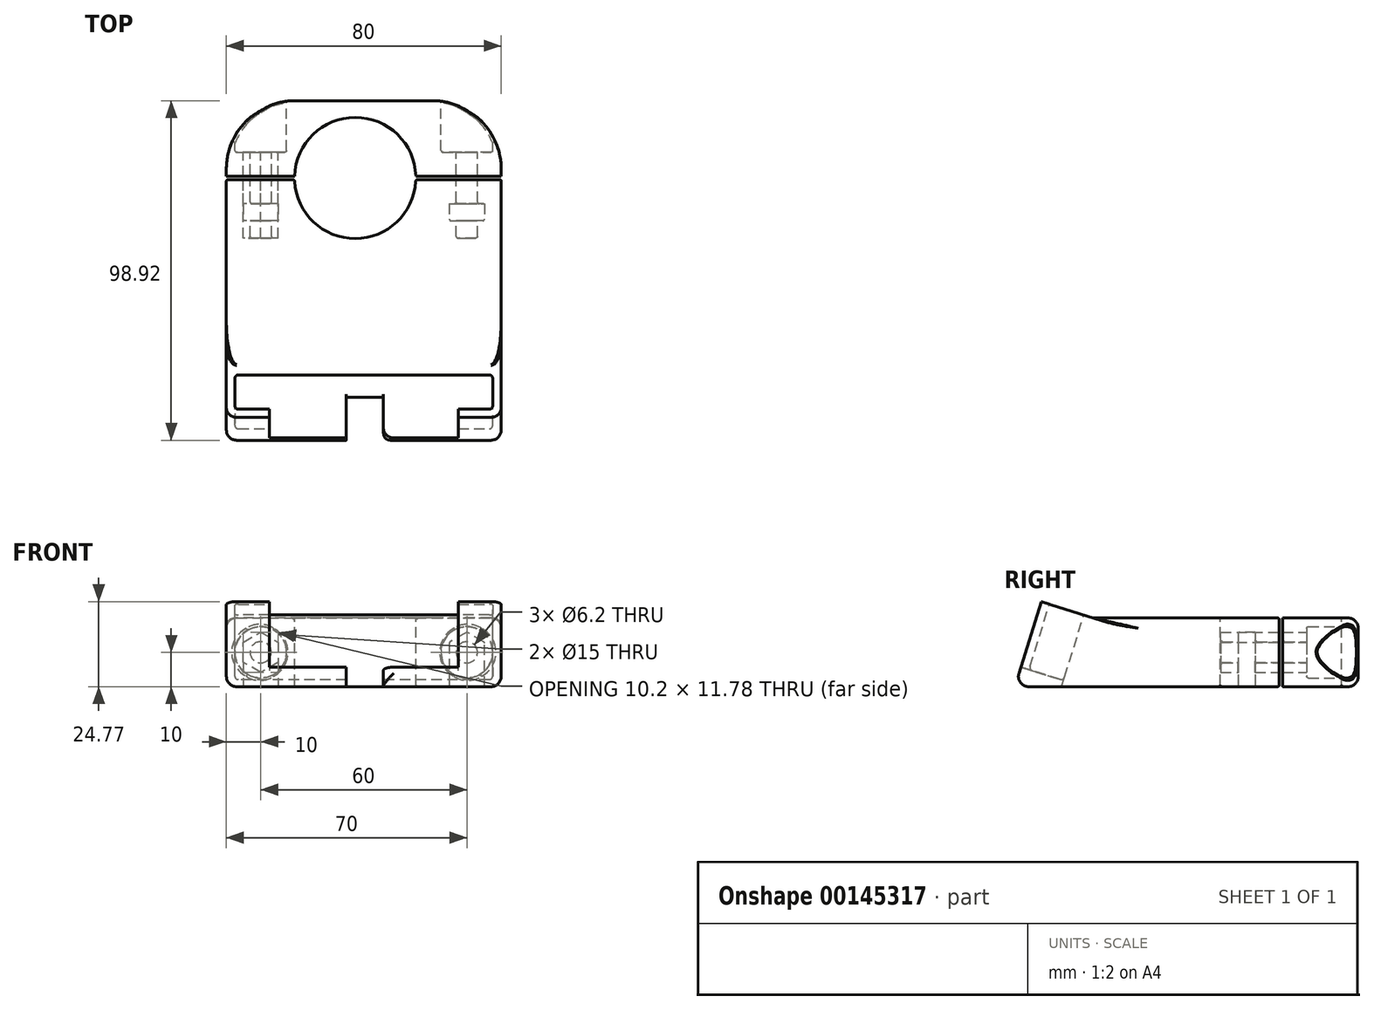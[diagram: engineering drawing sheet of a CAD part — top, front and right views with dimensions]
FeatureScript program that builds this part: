
annotation { "Feature Type Name" : "Feature", "Feature Type Description" : "" }
export const myFeature = defineFeature(function(context is Context, id is Id, definition is map)
    precondition{}
    {
        {
            var Q0;
            Q0=qCreatedBy(makeId("Right.planeOp"),FACE);
            var sketch = newSketch(context, id + "F0", { "sketchPlane" : qUnion([Q0])});
            skLineSegment(sketch, "E0", {"start": v(-34.54, 0) * mm, "end": v(65.46, 0) * mm});
            skLineSegment(sketch, "E1", {"start": v(65.46, 0) * mm, "end": v(65.46, 20) * mm});
            skLineSegment(sketch, "E2", {"start": v(65.46, 20) * mm, "end": v(-11.54, 20) * mm});
            skLineSegment(sketch, "E3", {"start": v(-11.54, 20) * mm, "end": v(-26.81, 24.77) * mm});
            skLineSegment(sketch, "E4", {"start": v(-26.81, 24.77) * mm, "end": v(-34.54, 0) * mm});
            skLineSegment(sketch, "E5", {"start": v(25.46, 20) * mm, "end": v(25.46, 148.67) * mm});
            skLineSegment(sketch, "E6", {"start": v(-14.4, 20.9) * mm, "end": v(40.27, 196.16) * mm});
            skSolve(sketch);
        }
        {
            var Q0;
            Q0=makeQuery(id+"F0.imprint","IMPRINT",FACE,{"disambiguationData":[TD([[makeQuery(id+"F0.imprint","IMPRINT",EDGE,{"derivedFrom":sQuery(id+"F0.wireOp",EDGE,"E0")}),1.0]])]});
            extrude(context, id + "F1", {"entities" : qUnion([Q0]), "endBound" : BoundingType.SYMMETRIC, "depth" : 80 * mm});
        }
        {
            var Q0;
            Q0=makeQuery(id+"F1.opExtrude","SWEPT_FACE",FACE,{"disambiguationData":[OSD([sQuery(id+"F0.wireOp",EDGE,"E3")])]});
            var sketch = newSketch(context, id + "F2", { "sketchPlane" : qUnion([Q0])});
            skLineSegment(sketch, "E7", {"start": v(-37.5, -19.97) * mm, "end": v(-37.5, -30.47) * mm});
            skLineSegment(sketch, "E8", {"start": v(-37.5, -30.47) * mm, "end": v(37.5, -30.47) * mm});
            skLineSegment(sketch, "E9", {"start": v(37.5, -30.47) * mm, "end": v(37.5, -19.97) * mm});
            skLineSegment(sketch, "E10", {"start": v(37.5, -19.97) * mm, "end": v(-37.5, -19.97) * mm});
            skLineSegment(sketch, "E11", {"start": v(-27.5, -32.97) * mm, "end": v(-27.5, -30.47) * mm});
            skLineSegment(sketch, "E12", {"start": v(-27.5, -30.47) * mm, "end": v(27.5, -30.47) * mm});
            skLineSegment(sketch, "E13", {"start": v(27.5, -30.47) * mm, "end": v(27.5, -32.97) * mm});
            skLineSegment(sketch, "E14", {"start": v(27.5, -32.97) * mm, "end": v(-27.5, -32.97) * mm});
            skSolve(sketch);
        }
        {
            var Q0;
            Q0=makeQuery(id+"F2.imprint","IMPRINT",FACE,{"disambiguationData":[TD([[makeQuery(id+"F2.imprint","IMPRINT",EDGE,{"derivedFrom":sQuery(id+"F2.wireOp",EDGE,"E7")}),1.0]])]});
            extrude(context, id + "F3", {"entities" : qUnion([Q0]), "operationType" : NewBodyOperationType.REMOVE, "oppositeDirection" : true, "depth" : 20 * mm});
        }
        {
            var Q0;
            Q0=makeQuery(id+"F2.imprint","IMPRINT",FACE,{"disambiguationData":[TD([[makeQuery(id+"F2.imprint","IMPRINT",EDGE,{"derivedFrom":sQuery(id+"F2.wireOp",EDGE,"E11")}),-1.0]])]});
            extrude(context, id + "F4", {"entities" : qUnion([Q0]), "operationType" : NewBodyOperationType.REMOVE, "oppositeDirection" : true, "depth" : 20 * mm});
        }
        {
            var Q0;
            {var subQ0=sQuery(id+"F2.wireOp",EDGE,"E12");Q0=makeQuery(id+"F4.boolean.opBoolean","MERGE",FACE,{"derivedFrom":[makeQuery(id+"F3.boolean.opBoolean","COPY",FACE,{"derivedFrom":makeQuery(id+"F3.opExtrude","CAP_FACE",FACE,{"disambiguationData":[OSD([sQuery(id+"F2.wireOp",EDGE,"E7"),sQuery(id+"F2.wireOp",EDGE,"E8"),sQuery(id+"F2.wireOp",EDGE,"E9"),sQuery(id+"F2.wireOp",EDGE,"E10"),subQ0])],"isStart":false})}),makeQuery(id+"F4.opExtrude","CAP_FACE",FACE,{"disambiguationData":[OSD([sQuery(id+"F2.wireOp",EDGE,"E11"),subQ0,sQuery(id+"F2.wireOp",EDGE,"E13"),sQuery(id+"F2.wireOp",EDGE,"E14")])],"isStart":false})]});}
            var sketch = newSketch(context, id + "F5", { "sketchPlane" : qUnion([Q0])});
            skLineSegment(sketch, "E15", {"start": v(-5.1, -32.97) * mm, "end": v(-5.1, -19.97) * mm});
            skLineSegment(sketch, "E16", {"start": v(-5.1, -19.97) * mm, "end": v(5.72, -19.97) * mm});
            skLineSegment(sketch, "E17", {"start": v(5.72, -19.97) * mm, "end": v(5.72, -32.97) * mm});
            skLineSegment(sketch, "E18", {"start": v(5.72, -32.97) * mm, "end": v(-5.1, -32.97) * mm});
            skSolve(sketch);
        }
        {
            var Q0;
            Q0=makeQuery(id+"F5.imprint","IMPRINT",FACE,{"disambiguationData":[TD([[makeQuery(id+"F5.imprint","IMPRINT",EDGE,{"derivedFrom":sQuery(id+"F5.wireOp",EDGE,"E15")}),-1.0]])]});
            extrude(context, id + "F6", {"entities" : qUnion([Q0]), "operationType" : NewBodyOperationType.REMOVE, "oppositeDirection" : true, "depth" : 25 * mm});
        }
        {
            var Q0;
            Q0=makeQuery(id+"F1.opExtrude","SWEPT_FACE",FACE,{"disambiguationData":[OSD([sQuery(id+"F0.wireOp",EDGE,"E2")])]});
            var sketch = newSketch(context, id + "F7", { "sketchPlane" : qUnion([Q0])});
            skCircle(sketch, "E19", {"center": v(-2.5, 42.96) * mm, "radius": 17.65 * mm});
            skLineSegment(sketch, "E20", {"start": v(-40, 43.46) * mm, "end": v(40, 43.46) * mm});
            skLineSegment(sketch, "E21", {"start": v(-40, 42.46) * mm, "end": v(40, 42.46) * mm});
            skSolve(sketch);
        }
        {
            var Q0;
            {var subQ0=sQuery(id+"F7.wireOp",EDGE,"E21");var subQ1=sQuery(id+"F7.wireOp",EDGE,"E19");var subQ2=makeQuery(id+"F7.imprint","INTERSECT",VERTEX,{"disambiguationData":[OD(0.0)],"derivedFrom":[subQ1,subQ0]});Q0=makeQuery(id+"F7.imprint","IMPRINT",FACE,{"disambiguationData":[TD([[makeQuery(id+"F7.imprint","IMPRINT",EDGE,{"disambiguationData":[TD([[subQ2,-1.0]])],"derivedFrom":subQ1}),1.0]])]});}
            var Q1;
            {var subQ0=sQuery(id+"F7.wireOp",EDGE,"E20");var subQ1=sQuery(id+"F7.wireOp",EDGE,"E19");var subQ2=makeQuery(id+"F7.imprint","INTERSECT",VERTEX,{"disambiguationData":[OD(0.0)],"derivedFrom":[subQ1,subQ0]});Q1=makeQuery(id+"F7.imprint","IMPRINT",FACE,{"disambiguationData":[TD([[makeQuery(id+"F7.imprint","IMPRINT",EDGE,{"disambiguationData":[TD([[subQ2,1.0]])],"derivedFrom":subQ1}),1.0]])]});}
            var Q2;
            {var subQ0=sQuery(id+"F7.wireOp",EDGE,"E20");var subQ1=sQuery(id+"F7.wireOp",EDGE,"E19");var subQ2=makeQuery(id+"F7.imprint","INTERSECT",VERTEX,{"disambiguationData":[OD(0.0)],"derivedFrom":[subQ1,subQ0]});Q2=makeQuery(id+"F7.imprint","IMPRINT",FACE,{"disambiguationData":[TD([[makeQuery(id+"F7.imprint","IMPRINT",EDGE,{"disambiguationData":[TD([[subQ2,-1.0]])],"derivedFrom":subQ1}),1.0]])]});}
            extrude(context, id + "F8", {"entities" : qUnion([Q0, Q1, Q2]), "operationType" : NewBodyOperationType.REMOVE, "oppositeDirection" : true, "depth" : 25 * mm});
        }
        {
            var Q0;
            Q0=makeQuery(id+"F1.opExtrude","SWEPT_FACE",FACE,{"disambiguationData":[OSD([sQuery(id+"F0.wireOp",EDGE,"E1")])]});
            var sketch = newSketch(context, id + "F9", { "sketchPlane" : qUnion([Q0])});
            skCircle(sketch, "E22", {"center": v(-30, 10) * mm, "radius": 3.1 * mm});
            skPoint(sketch, "E22.centerSnap0", {"position": v(-40, 10) * mm});
            skLineSegment(sketch, "E23", {"start": v(0, 0) * mm, "end": v(0, 27.17) * mm});
            skPoint(sketch, "E23.endSnap0", {"position": v(0, 20) * mm});
            skCircle(sketch, "E24", {"center": v(-30, 10) * mm, "radius": 7.5 * mm});
            skCircle(sketch, "E25.cCircle", {"center": v(-30, 10) * mm, "radius": 5.1 * mm, "construction": true});
            skLineSegment(sketch, "E25.0", {"start": v(-24.9, 12.94) * mm, "end": v(-24.9, 7.06) * mm});
            skLineSegment(sketch, "E25.1", {"start": v(-24.9, 7.06) * mm, "end": v(-30, 4.11) * mm});
            skLineSegment(sketch, "E25.2", {"start": v(-30, 4.11) * mm, "end": v(-35.1, 7.06) * mm});
            skLineSegment(sketch, "E25.3", {"start": v(-35.1, 7.06) * mm, "end": v(-35.1, 12.94) * mm});
            skLineSegment(sketch, "E25.4", {"start": v(-35.1, 12.94) * mm, "end": v(-30, 15.89) * mm});
            skLineSegment(sketch, "E25.5", {"start": v(-30, 15.89) * mm, "end": v(-24.9, 12.94) * mm});
            skPoint(sketch, "E25.0.midPoint", {"position": v(-24.9, 10) * mm});
            skCircle(sketch, "E26.MirrorC", {"center": v(30, 10) * mm, "radius": 3.1 * mm});
            skCircle(sketch, "E27.MirrorC", {"center": v(30, 10) * mm, "radius": 5.1 * mm, "construction": true});
            skLineSegment(sketch, "E28.MirrorCS", {"start": v(24.9, 7.06) * mm, "end": v(30, 4.11) * mm});
            skLineSegment(sketch, "E29.MirrorCS", {"start": v(24.9, 12.94) * mm, "end": v(24.9, 7.06) * mm});
            skLineSegment(sketch, "E30.MirrorCS", {"start": v(30, 15.89) * mm, "end": v(24.9, 12.94) * mm});
            skLineSegment(sketch, "E31.MirrorCS", {"start": v(35.1, 12.94) * mm, "end": v(30, 15.89) * mm});
            skLineSegment(sketch, "E32.MirrorCS", {"start": v(35.1, 7.06) * mm, "end": v(35.1, 12.94) * mm});
            skLineSegment(sketch, "E33.MirrorCS", {"start": v(30, 4.11) * mm, "end": v(35.1, 7.06) * mm});
            skCircle(sketch, "E34.MirrorC", {"center": v(30, 10) * mm, "radius": 7.5 * mm});
            skSolve(sketch);
        }
        {
            var Q0;
            Q0=makeQuery(id+"F9.imprint","IMPRINT",FACE,{"disambiguationData":[TD([[makeQuery(id+"F9.imprint","IMPRINT",EDGE,{"derivedFrom":sQuery(id+"F9.wireOp",EDGE,"E22")}),1.0]])]});
            var Q1;
            Q1=makeQuery(id+"F9.imprint","IMPRINT",FACE,{"disambiguationData":[TD([[makeQuery(id+"F9.imprint","IMPRINT",EDGE,{"derivedFrom":sQuery(id+"F9.wireOp",EDGE,"E26.MirrorC")}),-1.0]])]});
            extrude(context, id + "F10", {"entities" : qUnion([Q0, Q1]), "operationType" : NewBodyOperationType.REMOVE, "oppositeDirection" : true, "depth" : 40 * mm});
        }
        {
            var Q0;
            Q0=makeQuery(id+"F9.imprint","IMPRINT",FACE,{"disambiguationData":[TD([[makeQuery(id+"F9.imprint","IMPRINT",EDGE,{"derivedFrom":sQuery(id+"F9.wireOp",EDGE,"E22")}),-1.0]])]});
            var Q1;
            Q1=makeQuery(id+"F9.imprint","IMPRINT",FACE,{"disambiguationData":[TD([[makeQuery(id+"F9.imprint","IMPRINT",EDGE,{"derivedFrom":sQuery(id+"F9.wireOp",EDGE,"E26.MirrorC")}),1.0]])]});
            extrude(context, id + "F11", {"entities" : qUnion([Q0, Q1]), "operationType" : NewBodyOperationType.REMOVE, "oppositeDirection" : true, "depth" : 35 * mm});
        }
        {
            var Q0;
            Q0=makeQuery(id+"F9.imprint","IMPRINT",FACE,{"disambiguationData":[TD([[makeQuery(id+"F9.imprint","IMPRINT",EDGE,{"derivedFrom":sQuery(id+"F9.wireOp",EDGE,"E22")}),-1.0]])]});
            var Q1;
            Q1=makeQuery(id+"F9.imprint","IMPRINT",FACE,{"disambiguationData":[TD([[makeQuery(id+"F9.imprint","IMPRINT",EDGE,{"derivedFrom":sQuery(id+"F9.wireOp",EDGE,"E26.MirrorC")}),1.0]])]});
            extrude(context, id + "F12", {"entities" : qUnion([Q0, Q1]), "operationType" : NewBodyOperationType.ADD, "oppositeDirection" : true, "depth" : 30 * mm});
        }
        {
            var Q0;
            Q0=makeQuery(id+"F9.imprint","IMPRINT",FACE,{"disambiguationData":[TD([[makeQuery(id+"F9.imprint","IMPRINT",EDGE,{"derivedFrom":sQuery(id+"F9.wireOp",EDGE,"E24")}),1.0]])]});
            var Q1;
            Q1=makeQuery(id+"F9.imprint","IMPRINT",FACE,{"disambiguationData":[TD([[makeQuery(id+"F9.imprint","IMPRINT",EDGE,{"derivedFrom":sQuery(id+"F9.wireOp",EDGE,"E22")}),-1.0]])]});
            var Q2;
            Q2=makeQuery(id+"F9.imprint","IMPRINT",FACE,{"disambiguationData":[TD([[makeQuery(id+"F9.imprint","IMPRINT",EDGE,{"derivedFrom":sQuery(id+"F9.wireOp",EDGE,"E26.MirrorC")}),1.0]])]});
            var Q3;
            Q3=makeQuery(id+"F9.imprint","IMPRINT",FACE,{"disambiguationData":[TD([[makeQuery(id+"F9.imprint","IMPRINT",EDGE,{"derivedFrom":sQuery(id+"F9.wireOp",EDGE,"E28.MirrorCS")}),-1.0]])]});
            extrude(context, id + "F13", {"entities" : qUnion([Q0, Q1, Q2, Q3]), "operationType" : NewBodyOperationType.REMOVE, "oppositeDirection" : true, "depth" : 15 * mm});
        }
        {
            var Q0;
            Q0=makeQuery(id+"F1.opExtrude","SWEPT_FACE",FACE,{"disambiguationData":[OSD([sQuery(id+"F0.wireOp",EDGE,"E0")])]});
            var sketch = newSketch(context, id + "F14", { "sketchPlane" : qUnion([Q0])});
            skLineSegment(sketch, "E35.bottom", {"start": v(24.9, -35.46) * mm, "end": v(35.1, -35.46) * mm});
            skLineSegment(sketch, "E35.top", {"start": v(24.9, -30.46) * mm, "end": v(35.1, -30.46) * mm});
            skLineSegment(sketch, "E35.left", {"start": v(24.9, -35.46) * mm, "end": v(24.9, -30.46) * mm});
            skLineSegment(sketch, "E35.right", {"start": v(35.1, -35.46) * mm, "end": v(35.1, -30.46) * mm});
            skPoint(sketch, "E35.middle", {"position": v(30, -32.96) * mm});
            skLineSegment(sketch, "E36", {"start": v(0, -65.46) * mm, "end": v(0, 26.3) * mm});
            skLineSegment(sketch, "E37.MirrorCS", {"start": v(-24.9, -30.46) * mm, "end": v(-35.1, -30.46) * mm});
            skLineSegment(sketch, "E38.MirrorCS", {"start": v(-35.1, -35.46) * mm, "end": v(-35.1, -30.46) * mm});
            skLineSegment(sketch, "E39.MirrorCS", {"start": v(-24.9, -35.46) * mm, "end": v(-35.1, -35.46) * mm});
            skLineSegment(sketch, "E40.MirrorCS", {"start": v(-24.9, -35.46) * mm, "end": v(-24.9, -30.46) * mm});
            skSolve(sketch);
        }
        {
            var Q0;
            Q0=makeQuery(id+"F14.imprint","IMPRINT",FACE,{"disambiguationData":[TD([[makeQuery(id+"F14.imprint","IMPRINT",EDGE,{"derivedFrom":sQuery(id+"F14.wireOp",EDGE,"E37.MirrorCS")}),1.0]])]});
            var Q1;
            Q1=makeQuery(id+"F14.imprint","IMPRINT",FACE,{"disambiguationData":[TD([[makeQuery(id+"F14.imprint","IMPRINT",EDGE,{"derivedFrom":sQuery(id+"F14.wireOp",EDGE,"E35.bottom")}),1.0]])]});
            extrude(context, id + "F15", {"entities" : qUnion([Q0, Q1]), "operationType" : NewBodyOperationType.REMOVE, "oppositeDirection" : true, "depth" : 10 * mm});
        }
        {
            var Q0;
            {var subQ0=sQuery(id+"F7.wireOp",EDGE,"E20");var subQ1=sQuery(id+"F7.wireOp",EDGE,"E19");var subQ2=makeQuery(id+"F7.imprint","INTERSECT",VERTEX,{"disambiguationData":[OD(1.0)],"derivedFrom":[subQ1,subQ0]});Q0=makeQuery(id+"F7.imprint","IMPRINT",FACE,{"disambiguationData":[TD([[makeQuery(id+"F7.imprint","IMPRINT",EDGE,{"disambiguationData":[TD([[subQ2,1.0]])],"derivedFrom":subQ1}),-1.0]])]});}
            var Q1;
            {var subQ0=sQuery(id+"F7.wireOp",EDGE,"E20");var subQ1=sQuery(id+"F7.wireOp",EDGE,"E19");var subQ2=makeQuery(id+"F7.imprint","INTERSECT",VERTEX,{"disambiguationData":[OD(0.0)],"derivedFrom":[subQ1,subQ0]});Q1=makeQuery(id+"F7.imprint","IMPRINT",FACE,{"disambiguationData":[TD([[makeQuery(id+"F7.imprint","IMPRINT",EDGE,{"disambiguationData":[TD([[subQ2,-1.0]])],"derivedFrom":subQ1}),-1.0]])]});}
            extrude(context, id + "F16", {"entities" : qUnion([Q0, Q1]), "operationType" : NewBodyOperationType.REMOVE, "endBound" : BoundingType.THROUGH_ALL, "oppositeDirection" : true, "depth" : 25 * mm});
        }
        {
            var Q0;
            Q0=makeQuery(id+"F1.opExtrude","CAP_EDGE",EDGE,{"disambiguationData":[OSD([sQuery(id+"F0.wireOp",EDGE,"E1")])],"isStart":false});
            var Q1;
            Q1=makeQuery(id+"F1.opExtrude","CAP_EDGE",EDGE,{"disambiguationData":[OSD([sQuery(id+"F0.wireOp",EDGE,"E1")])],"isStart":true});
            fillet(context, id + "F17", {"entities" : qUnion([Q0, Q1]), "radius" : 20 * mm, "tangentPropagation" : true, "allowEdgeOverflow" : false});
        }
        {
            var Q0;
            {var subQ0=sQuery(id+"F0.wireOp",EDGE,"E3");var subQ1=sQuery(id+"F0.wireOp",EDGE,"E2");var subQ3=makeQuery(id+"F1.opExtrude","CAP_EDGE",EDGE,{"disambiguationData":[OSD([subQ1])],"isStart":false});Q0=makeQuery(id+"F16.boolean.opBoolean","SPLIT",EDGE,{"disambiguationData":[TD([makeQuery(id+"F1.opExtrude","SWEPT_FACE",FACE,{"disambiguationData":[OSD([subQ0])]})])],"derivedFrom":subQ3});}
            var Q1;
            {var subQ1=sQuery(id+"F0.wireOp",EDGE,"E2");var subQ2=makeQuery(id+"F1.opExtrude","CAP_EDGE",EDGE,{"disambiguationData":[OSD([subQ1])],"isStart":false});var subQ3=sQuery(id+"F0.wireOp",EDGE,"E1");Q1=makeQuery(id+"F16.boolean.opBoolean","SPLIT",EDGE,{"disambiguationData":[TD([makeQuery(id+"F1.opExtrude","SWEPT_FACE",FACE,{"disambiguationData":[OSD([subQ3])]})])],"derivedFrom":subQ2});}
            var Q2;
            {var subQ1=sQuery(id+"F0.wireOp",EDGE,"E1");var subQ3=sQuery(id+"F0.wireOp",EDGE,"E2");Q2=makeQuery(id+"F17.opFillet","BLEND_EDGE",EDGE,{"blendedFrom":[makeQuery(id+"F1.opExtrude","CAP_EDGE",EDGE,{"disambiguationData":[OSD([subQ1])],"isStart":false}),makeQuery(id+"F16.boolean.opBoolean","SPLIT",FACE,{"disambiguationData":[TD([makeQuery(id+"F1.opExtrude","SWEPT_FACE",FACE,{"disambiguationData":[OSD([subQ1])]})])],"derivedFrom":makeQuery(id+"F1.opExtrude","SWEPT_FACE",FACE,{"disambiguationData":[OSD([subQ3])]})})],"blendedInto":[makeQuery(id+"F16.boolean.opBoolean","SPLIT",FACE,{"disambiguationData":[TD([makeQuery(id+"F1.opExtrude","SWEPT_FACE",FACE,{"disambiguationData":[OSD([subQ1])]})])],"derivedFrom":makeQuery(id+"F1.opExtrude","SWEPT_FACE",FACE,{"disambiguationData":[OSD([subQ3])]})})]});}
            var Q3;
            {var subQ0=sQuery(id+"F0.wireOp",EDGE,"E3");var subQ1=sQuery(id+"F0.wireOp",EDGE,"E2");var subQ3=makeQuery(id+"F1.opExtrude","CAP_EDGE",EDGE,{"disambiguationData":[OSD([subQ1])],"isStart":true});Q3=makeQuery(id+"F16.boolean.opBoolean","SPLIT",EDGE,{"disambiguationData":[TD([makeQuery(id+"F1.opExtrude","SWEPT_FACE",FACE,{"disambiguationData":[OSD([subQ0])]})])],"derivedFrom":subQ3});}
            var Q4;
            Q4=makeQuery(id+"F6.boolean.opBoolean","COPY",EDGE,{"derivedFrom":makeQuery(id+"F6.opExtrude","SWEPT_EDGE",EDGE,{"disambiguationData":[OSD([sQuery(id+"F2.wireOp",EDGE,"E14"),sQuery(id+"F5.wireOp",EDGE,"E15"),sQuery(id+"F5.wireOp",EDGE,"E18")])]})});
            var Q5;
            Q5=makeQuery(id+"F6.boolean.opBoolean","COPY",EDGE,{"derivedFrom":makeQuery(id+"F6.opExtrude","SWEPT_EDGE",EDGE,{"disambiguationData":[OSD([sQuery(id+"F2.wireOp",EDGE,"E14"),sQuery(id+"F5.wireOp",EDGE,"E17"),sQuery(id+"F5.wireOp",EDGE,"E18")])]})});
            var Q6;
            Q6=makeQuery(id+"F4.boolean.opBoolean","COPY",EDGE,{"derivedFrom":makeQuery(id+"F4.opExtrude","CAP_EDGE",EDGE,{"disambiguationData":[OSD([sQuery(id+"F2.wireOp",EDGE,"E13")])],"isStart":true})});
            var Q7;
            Q7=makeQuery(id+"F4.boolean.opBoolean","COPY",EDGE,{"derivedFrom":makeQuery(id+"F4.opExtrude","CAP_EDGE",EDGE,{"disambiguationData":[OSD([sQuery(id+"F2.wireOp",EDGE,"E11")])],"isStart":true})});
            var Q8;
            {var subQ0=sQuery(id+"F0.wireOp",EDGE,"E0");var subQ1=sQuery(id+"F0.wireOp",EDGE,"E4");Q8=makeQuery(id+"F6.boolean.opBoolean","SPLIT",EDGE,{"disambiguationData":[TD([makeQuery(id+"F6.opExtrude","SWEPT_FACE",FACE,{"disambiguationData":[OSD([sQuery(id+"F5.wireOp",EDGE,"E15")])]})])],"derivedFrom":makeQuery(id+"F1.opExtrude","SWEPT_EDGE",EDGE,{"disambiguationData":[OSD([subQ0,subQ1])]})});}
            var Q9;
            {var subQ0=sQuery(id+"F0.wireOp",EDGE,"E0");var subQ1=sQuery(id+"F0.wireOp",EDGE,"E4");Q9=makeQuery(id+"F6.boolean.opBoolean","SPLIT",EDGE,{"disambiguationData":[TD([makeQuery(id+"F6.opExtrude","SWEPT_FACE",FACE,{"disambiguationData":[OSD([sQuery(id+"F5.wireOp",EDGE,"E17")])]})])],"derivedFrom":makeQuery(id+"F1.opExtrude","SWEPT_EDGE",EDGE,{"disambiguationData":[OSD([subQ0,subQ1])]})});}
            var Q10;
            {var subQ0=sQuery(id+"F0.wireOp",EDGE,"E0");var subQ1=sQuery(id+"F0.wireOp",EDGE,"E4");Q10=makeQuery(id+"F16.boolean.opBoolean","SPLIT",EDGE,{"disambiguationData":[TD([makeQuery(id+"F1.opExtrude","SWEPT_FACE",FACE,{"disambiguationData":[OSD([subQ1])]})])],"derivedFrom":makeQuery(id+"F1.opExtrude","CAP_EDGE",EDGE,{"disambiguationData":[OSD([subQ0])],"isStart":true})});}
            var Q11;
            {var subQ0=sQuery(id+"F0.wireOp",EDGE,"E0");var subQ1=sQuery(id+"F0.wireOp",EDGE,"E4");Q11=makeQuery(id+"F16.boolean.opBoolean","SPLIT",EDGE,{"disambiguationData":[TD([makeQuery(id+"F1.opExtrude","SWEPT_FACE",FACE,{"disambiguationData":[OSD([subQ1])]})])],"derivedFrom":makeQuery(id+"F1.opExtrude","CAP_EDGE",EDGE,{"disambiguationData":[OSD([subQ0])],"isStart":false})});}
            var Q12;
            {var subQ2=sQuery(id+"F0.wireOp",EDGE,"E1");var subQ3=sQuery(id+"F0.wireOp",EDGE,"E0");Q12=makeQuery(id+"F16.boolean.opBoolean","SPLIT",EDGE,{"disambiguationData":[TD([makeQuery(id+"F1.opExtrude","SWEPT_FACE",FACE,{"disambiguationData":[OSD([subQ2])]})])],"derivedFrom":makeQuery(id+"F1.opExtrude","CAP_EDGE",EDGE,{"disambiguationData":[OSD([subQ3])],"isStart":false})});}
            var Q13;
            Q13=makeQuery(id+"F1.opExtrude","CAP_EDGE",EDGE,{"disambiguationData":[OSD([sQuery(id+"F0.wireOp",EDGE,"E4")])],"isStart":false});
            var Q14;
            Q14=makeQuery(id+"F1.opExtrude","CAP_EDGE",EDGE,{"disambiguationData":[OSD([sQuery(id+"F0.wireOp",EDGE,"E4")])],"isStart":true});
            fillet(context, id + "F18", {"entities" : qUnion([Q0, Q1, Q2, Q3, Q4, Q5, Q6, Q7, Q8, Q9, Q10, Q11, Q12, Q13, Q14]), "radius" : 3 * mm, "tangentPropagation" : true, "allowEdgeOverflow" : false});
        }
        {
            var Q0;
            {var subQ0=sQuery(id+"F7.wireOp",EDGE,"E20");Q0=makeQuery(id+"F16.boolean.opBoolean","COPY",EDGE,{"derivedFrom":makeQuery(id+"F16.opExtrude","CAP_EDGE",EDGE,{"disambiguationData":[OSD([subQ0]),TDD([makeQuery(id+"F7.imprint","IMPRINT",EDGE,{"disambiguationData":[TD([[makeQuery(id+"F7.imprint","INTERSECT",VERTEX,{"derivedFrom":[makeQuery(id+"F1.opExtrude","CAP_EDGE",EDGE,{"disambiguationData":[OSD([sQuery(id+"F0.wireOp",EDGE,"E2")])],"isStart":true}),subQ0]}),-1.0]])],"derivedFrom":subQ0})])],"isStart":true})});}
            var Q1;
            {var subQ0=sQuery(id+"F7.wireOp",EDGE,"E20");var subQ1=sQuery(id+"F7.wireOp",EDGE,"E19");Q1=makeQuery(id+"F16.boolean.opBoolean","COPY",EDGE,{"derivedFrom":makeQuery(id+"F16.opExtrude","SWEPT_EDGE",EDGE,{"disambiguationData":[OSD([subQ1,subQ0]),TDD([makeQuery(id+"F7.imprint","INTERSECT",VERTEX,{"disambiguationData":[OD(0.0)],"derivedFrom":[subQ1,subQ0]})])]})});}
            var Q2;
            {var subQ0=sQuery(id+"F7.wireOp",EDGE,"E20");var subQ1=sQuery(id+"F7.wireOp",EDGE,"E19");Q2=makeQuery(id+"F16.boolean.opBoolean","COPY",EDGE,{"derivedFrom":makeQuery(id+"F16.opExtrude","SWEPT_EDGE",EDGE,{"disambiguationData":[OSD([subQ1,subQ0]),TDD([makeQuery(id+"F7.imprint","INTERSECT",VERTEX,{"disambiguationData":[OD(1.0)],"derivedFrom":[subQ1,subQ0]})])]})});}
            var Q3;
            {var subQ0=sQuery(id+"F7.wireOp",EDGE,"E20");Q3=makeQuery(id+"F16.boolean.opBoolean","COPY",EDGE,{"derivedFrom":makeQuery(id+"F16.opExtrude","CAP_EDGE",EDGE,{"disambiguationData":[OSD([subQ0]),TDD([makeQuery(id+"F7.imprint","IMPRINT",EDGE,{"disambiguationData":[TD([[makeQuery(id+"F7.imprint","INTERSECT",VERTEX,{"derivedFrom":[makeQuery(id+"F1.opExtrude","CAP_EDGE",EDGE,{"disambiguationData":[OSD([sQuery(id+"F0.wireOp",EDGE,"E2")])],"isStart":false}),subQ0]}),1.0]])],"derivedFrom":subQ0})])],"isStart":true})});}
            var Q4;
            {var subQ0=sQuery(id+"F7.wireOp",EDGE,"E21");var subQ1=sQuery(id+"F0.wireOp",EDGE,"E2");Q4=makeQuery(id+"F16.boolean.opBoolean","COPY",EDGE,{"derivedFrom":makeQuery(id+"F16.opExtrude","SWEPT_EDGE",EDGE,{"disambiguationData":[OSD([subQ1,subQ0]),TDD([makeQuery(id+"F7.imprint","INTERSECT",VERTEX,{"derivedFrom":[makeQuery(id+"F1.opExtrude","CAP_EDGE",EDGE,{"disambiguationData":[OSD([subQ1])],"isStart":false}),subQ0]})])]})});}
            var Q5;
            {var subQ0=sQuery(id+"F7.wireOp",EDGE,"E21");var subQ1=sQuery(id+"F7.wireOp",EDGE,"E19");Q5=makeQuery(id+"F16.boolean.opBoolean","COPY",EDGE,{"derivedFrom":makeQuery(id+"F16.opExtrude","SWEPT_EDGE",EDGE,{"disambiguationData":[OSD([subQ1,subQ0]),TDD([makeQuery(id+"F7.imprint","INTERSECT",VERTEX,{"disambiguationData":[OD(1.0)],"derivedFrom":[subQ1,subQ0]})])]})});}
            var Q6;
            {var subQ0=sQuery(id+"F7.wireOp",EDGE,"E21");var subQ1=sQuery(id+"F7.wireOp",EDGE,"E19");Q6=makeQuery(id+"F16.boolean.opBoolean","COPY",EDGE,{"derivedFrom":makeQuery(id+"F16.opExtrude","SWEPT_EDGE",EDGE,{"disambiguationData":[OSD([subQ1,subQ0]),TDD([makeQuery(id+"F7.imprint","INTERSECT",VERTEX,{"disambiguationData":[OD(0.0)],"derivedFrom":[subQ1,subQ0]})])]})});}
            var Q7;
            {var subQ0=sQuery(id+"F7.wireOp",EDGE,"E21");Q7=makeQuery(id+"F16.boolean.opBoolean","INTERSECT",EDGE,{"derivedFrom":[makeQuery(id+"F1.opExtrude","SWEPT_FACE",FACE,{"disambiguationData":[OSD([sQuery(id+"F0.wireOp",EDGE,"E0")])]}),makeQuery(id+"F16.opExtrude","SWEPT_FACE",FACE,{"disambiguationData":[OSD([subQ0]),TDD([makeQuery(id+"F7.imprint","IMPRINT",EDGE,{"disambiguationData":[TD([[makeQuery(id+"F7.imprint","INTERSECT",VERTEX,{"derivedFrom":[makeQuery(id+"F1.opExtrude","CAP_EDGE",EDGE,{"disambiguationData":[OSD([sQuery(id+"F0.wireOp",EDGE,"E2")])],"isStart":true}),subQ0]}),-1.0]])],"derivedFrom":subQ0})])]})]});}
            var Q8;
            {var subQ0=makeQuery(id+"F1.opExtrude","SWEPT_FACE",FACE,{"disambiguationData":[OSD([sQuery(id+"F0.wireOp",EDGE,"E0")])]});var subQ1=sQuery(id+"F7.wireOp",EDGE,"E19");var subQ2=makeQuery(id+"F8.opExtrude","SWEPT_FACE",FACE,{"disambiguationData":[OSD([subQ1])]});var subQ3=sQuery(id+"F7.wireOp",EDGE,"E20");var subQ4=sQuery(id+"F0.wireOp",EDGE,"E2");Q8=makeQuery(id+"F16.boolean.opBoolean","SPLIT",EDGE,{"disambiguationData":[TD([makeQuery(id+"F16.opExtrude","SWEPT_FACE",FACE,{"disambiguationData":[OSD([subQ3]),TDD([makeQuery(id+"F7.imprint","IMPRINT",EDGE,{"disambiguationData":[TD([[makeQuery(id+"F7.imprint","INTERSECT",VERTEX,{"derivedFrom":[makeQuery(id+"F1.opExtrude","CAP_EDGE",EDGE,{"disambiguationData":[OSD([subQ4])],"isStart":true}),subQ3]}),-1.0]])],"derivedFrom":subQ3})])]})])],"derivedFrom":makeQuery(id+"F8.boolean.opBoolean","INTERSECT",EDGE,{"derivedFrom":[subQ0,subQ2]})});}
            var Q9;
            {var subQ0=makeQuery(id+"F1.opExtrude","SWEPT_FACE",FACE,{"disambiguationData":[OSD([sQuery(id+"F0.wireOp",EDGE,"E0")])]});var subQ1=sQuery(id+"F7.wireOp",EDGE,"E19");var subQ2=makeQuery(id+"F8.opExtrude","SWEPT_FACE",FACE,{"disambiguationData":[OSD([subQ1])]});var subQ3=sQuery(id+"F7.wireOp",EDGE,"E21");var subQ4=sQuery(id+"F0.wireOp",EDGE,"E2");Q9=makeQuery(id+"F16.boolean.opBoolean","SPLIT",EDGE,{"disambiguationData":[TD([makeQuery(id+"F16.opExtrude","SWEPT_FACE",FACE,{"disambiguationData":[OSD([subQ3]),TDD([makeQuery(id+"F7.imprint","IMPRINT",EDGE,{"disambiguationData":[TD([[makeQuery(id+"F7.imprint","INTERSECT",VERTEX,{"derivedFrom":[makeQuery(id+"F1.opExtrude","CAP_EDGE",EDGE,{"disambiguationData":[OSD([subQ4])],"isStart":true}),subQ3]}),-1.0]])],"derivedFrom":subQ3})])]})])],"derivedFrom":makeQuery(id+"F8.boolean.opBoolean","INTERSECT",EDGE,{"derivedFrom":[subQ0,subQ2]})});}
            var Q10;
            Q10=makeQuery(id+"F15.boolean.opBoolean","COPY",EDGE,{"derivedFrom":makeQuery(id+"F15.opExtrude","CAP_EDGE",EDGE,{"disambiguationData":[OSD([sQuery(id+"F14.wireOp",EDGE,"E37.MirrorCS")])],"isStart":true})});
            var Q11;
            Q11=makeQuery(id+"F15.boolean.opBoolean","COPY",EDGE,{"derivedFrom":makeQuery(id+"F15.opExtrude","CAP_EDGE",EDGE,{"disambiguationData":[OSD([sQuery(id+"F14.wireOp",EDGE,"E40.MirrorCS")])],"isStart":true})});
            var Q12;
            Q12=makeQuery(id+"F15.boolean.opBoolean","COPY",EDGE,{"derivedFrom":makeQuery(id+"F15.opExtrude","CAP_EDGE",EDGE,{"disambiguationData":[OSD([sQuery(id+"F14.wireOp",EDGE,"E39.MirrorCS")])],"isStart":true})});
            var Q13;
            Q13=makeQuery(id+"F15.boolean.opBoolean","COPY",EDGE,{"derivedFrom":makeQuery(id+"F15.opExtrude","CAP_EDGE",EDGE,{"disambiguationData":[OSD([sQuery(id+"F14.wireOp",EDGE,"E38.MirrorCS")])],"isStart":true})});
            var Q14;
            Q14=makeQuery(id+"F15.boolean.opBoolean","COPY",EDGE,{"derivedFrom":makeQuery(id+"F15.opExtrude","CAP_EDGE",EDGE,{"disambiguationData":[OSD([sQuery(id+"F14.wireOp",EDGE,"E35.bottom")])],"isStart":true})});
            var Q15;
            Q15=makeQuery(id+"F15.boolean.opBoolean","COPY",EDGE,{"derivedFrom":makeQuery(id+"F15.opExtrude","CAP_EDGE",EDGE,{"disambiguationData":[OSD([sQuery(id+"F14.wireOp",EDGE,"E35.left")])],"isStart":true})});
            var Q16;
            Q16=makeQuery(id+"F15.boolean.opBoolean","COPY",EDGE,{"derivedFrom":makeQuery(id+"F15.opExtrude","CAP_EDGE",EDGE,{"disambiguationData":[OSD([sQuery(id+"F14.wireOp",EDGE,"E35.top")])],"isStart":true})});
            var Q17;
            Q17=makeQuery(id+"F15.boolean.opBoolean","COPY",EDGE,{"derivedFrom":makeQuery(id+"F15.opExtrude","CAP_EDGE",EDGE,{"disambiguationData":[OSD([sQuery(id+"F14.wireOp",EDGE,"E35.right")])],"isStart":true})});
            var Q18;
            {var subQ0=sQuery(id+"F0.wireOp",EDGE,"E2");var subQ1=sQuery(id+"F7.wireOp",EDGE,"E19");var subQ2=sQuery(id+"F7.wireOp",EDGE,"E21");Q18=makeQuery(id+"F16.boolean.opBoolean","SPLIT",EDGE,{"disambiguationData":[TD([makeQuery(id+"F16.opExtrude","SWEPT_FACE",FACE,{"disambiguationData":[OSD([subQ2]),TDD([makeQuery(id+"F7.imprint","IMPRINT",EDGE,{"disambiguationData":[TD([[makeQuery(id+"F7.imprint","INTERSECT",VERTEX,{"derivedFrom":[makeQuery(id+"F1.opExtrude","CAP_EDGE",EDGE,{"disambiguationData":[OSD([subQ0])],"isStart":true}),subQ2]}),-1.0]])],"derivedFrom":subQ2})])]})])],"derivedFrom":makeQuery(id+"F8.boolean.opBoolean","COPY",EDGE,{"derivedFrom":makeQuery(id+"F8.opExtrude","CAP_EDGE",EDGE,{"disambiguationData":[OSD([subQ1])],"isStart":true})})});}
            var Q19;
            {var subQ0=sQuery(id+"F0.wireOp",EDGE,"E2");var subQ1=sQuery(id+"F7.wireOp",EDGE,"E19");var subQ2=sQuery(id+"F7.wireOp",EDGE,"E20");Q19=makeQuery(id+"F16.boolean.opBoolean","SPLIT",EDGE,{"disambiguationData":[TD([makeQuery(id+"F16.opExtrude","SWEPT_FACE",FACE,{"disambiguationData":[OSD([subQ2]),TDD([makeQuery(id+"F7.imprint","IMPRINT",EDGE,{"disambiguationData":[TD([[makeQuery(id+"F7.imprint","INTERSECT",VERTEX,{"derivedFrom":[makeQuery(id+"F1.opExtrude","CAP_EDGE",EDGE,{"disambiguationData":[OSD([subQ0])],"isStart":true}),subQ2]}),-1.0]])],"derivedFrom":subQ2})])]})])],"derivedFrom":makeQuery(id+"F8.boolean.opBoolean","COPY",EDGE,{"derivedFrom":makeQuery(id+"F8.opExtrude","CAP_EDGE",EDGE,{"disambiguationData":[OSD([subQ1])],"isStart":true})})});}
            var Q20;
            Q20=makeQuery(id+"F13.boolean.opBoolean","COPY",EDGE,{"derivedFrom":makeQuery(id+"F13.opExtrude","CAP_EDGE",EDGE,{"disambiguationData":[OSD([sQuery(id+"F9.wireOp",EDGE,"E22")])],"isStart":false})});
            var Q21;
            {var subQ1=sQuery(id+"F0.wireOp",EDGE,"E1");var subQ6=sQuery(id+"F0.wireOp",EDGE,"E0");Q21=makeQuery(id+"F18.opFillet","BLEND_EDGE",EDGE,{"blendedFrom":[makeQuery(id+"F17.opFillet","BLEND_EDGE",EDGE,{"blendedFrom":[makeQuery(id+"F1.opExtrude","CAP_EDGE",EDGE,{"disambiguationData":[OSD([subQ1])],"isStart":false}),makeQuery(id+"F16.boolean.opBoolean","SPLIT",FACE,{"disambiguationData":[TD([makeQuery(id+"F1.opExtrude","SWEPT_FACE",FACE,{"disambiguationData":[OSD([subQ1])]})])],"derivedFrom":makeQuery(id+"F1.opExtrude","SWEPT_FACE",FACE,{"disambiguationData":[OSD([subQ6])]})})],"blendedInto":[makeQuery(id+"F16.boolean.opBoolean","SPLIT",FACE,{"disambiguationData":[TD([makeQuery(id+"F1.opExtrude","SWEPT_FACE",FACE,{"disambiguationData":[OSD([subQ1])]})])],"derivedFrom":makeQuery(id+"F1.opExtrude","SWEPT_FACE",FACE,{"disambiguationData":[OSD([subQ6])]})})]}),makeQuery(id+"F13.boolean.opBoolean","COPY",FACE,{"derivedFrom":makeQuery(id+"F13.opExtrude","SWEPT_FACE",FACE,{"disambiguationData":[OSD([sQuery(id+"F9.wireOp",EDGE,"E24")])]})})],"blendedInto":[makeQuery(id+"F13.boolean.opBoolean","COPY",FACE,{"derivedFrom":makeQuery(id+"F13.opExtrude","SWEPT_FACE",FACE,{"disambiguationData":[OSD([sQuery(id+"F9.wireOp",EDGE,"E24")])]})})]});}
            var Q22;
            Q22=makeQuery(id+"F13.boolean.opBoolean","COPY",EDGE,{"derivedFrom":makeQuery(id+"F13.opExtrude","CAP_EDGE",EDGE,{"disambiguationData":[OSD([sQuery(id+"F9.wireOp",EDGE,"E26.MirrorC")])],"isStart":false})});
            var Q23;
            Q23=makeQuery(id+"F17.opFillet","BLEND_EDGE",EDGE,{"blendedFrom":[makeQuery(id+"F1.opExtrude","CAP_EDGE",EDGE,{"disambiguationData":[OSD([sQuery(id+"F0.wireOp",EDGE,"E1")])],"isStart":true}),makeQuery(id+"F13.boolean.opBoolean","COPY",FACE,{"derivedFrom":makeQuery(id+"F13.opExtrude","SWEPT_FACE",FACE,{"disambiguationData":[OSD([sQuery(id+"F9.wireOp",EDGE,"E34.MirrorC")])]})})],"blendedInto":[makeQuery(id+"F13.boolean.opBoolean","COPY",FACE,{"derivedFrom":makeQuery(id+"F13.opExtrude","SWEPT_FACE",FACE,{"disambiguationData":[OSD([sQuery(id+"F9.wireOp",EDGE,"E34.MirrorC")])]})})]});
            var Q24;
            {var subQ0=sQuery(id+"F7.wireOp",EDGE,"E20");Q24=makeQuery(id+"F16.boolean.opBoolean","INTERSECT",EDGE,{"derivedFrom":[makeQuery(id+"F12.opExtrude","SWEPT_FACE",FACE,{"disambiguationData":[OSD([sQuery(id+"F9.wireOp",EDGE,"E26.MirrorC")])]}),makeQuery(id+"F16.opExtrude","SWEPT_FACE",FACE,{"disambiguationData":[OSD([subQ0]),TDD([makeQuery(id+"F7.imprint","IMPRINT",EDGE,{"disambiguationData":[TD([[makeQuery(id+"F7.imprint","INTERSECT",VERTEX,{"derivedFrom":[makeQuery(id+"F1.opExtrude","CAP_EDGE",EDGE,{"disambiguationData":[OSD([sQuery(id+"F0.wireOp",EDGE,"E2")])],"isStart":true}),subQ0]}),-1.0]])],"derivedFrom":subQ0})])]})]});}
            var Q25;
            {var subQ0=sQuery(id+"F7.wireOp",EDGE,"E21");Q25=makeQuery(id+"F16.boolean.opBoolean","INTERSECT",EDGE,{"derivedFrom":[makeQuery(id+"F12.opExtrude","SWEPT_FACE",FACE,{"disambiguationData":[OSD([sQuery(id+"F9.wireOp",EDGE,"E26.MirrorC")])]}),makeQuery(id+"F16.opExtrude","SWEPT_FACE",FACE,{"disambiguationData":[OSD([subQ0]),TDD([makeQuery(id+"F7.imprint","IMPRINT",EDGE,{"disambiguationData":[TD([[makeQuery(id+"F7.imprint","INTERSECT",VERTEX,{"derivedFrom":[makeQuery(id+"F1.opExtrude","CAP_EDGE",EDGE,{"disambiguationData":[OSD([sQuery(id+"F0.wireOp",EDGE,"E2")])],"isStart":true}),subQ0]}),-1.0]])],"derivedFrom":subQ0})])]})]});}
            var Q26;
            {var subQ0=sQuery(id+"F7.wireOp",EDGE,"E20");Q26=makeQuery(id+"F16.boolean.opBoolean","INTERSECT",EDGE,{"derivedFrom":[makeQuery(id+"F12.opExtrude","SWEPT_FACE",FACE,{"disambiguationData":[OSD([sQuery(id+"F9.wireOp",EDGE,"E22")])]}),makeQuery(id+"F16.opExtrude","SWEPT_FACE",FACE,{"disambiguationData":[OSD([subQ0]),TDD([makeQuery(id+"F7.imprint","IMPRINT",EDGE,{"disambiguationData":[TD([[makeQuery(id+"F7.imprint","INTERSECT",VERTEX,{"derivedFrom":[makeQuery(id+"F1.opExtrude","CAP_EDGE",EDGE,{"disambiguationData":[OSD([sQuery(id+"F0.wireOp",EDGE,"E2")])],"isStart":false}),subQ0]}),1.0]])],"derivedFrom":subQ0})])]})]});}
            var Q27;
            {var subQ0=sQuery(id+"F7.wireOp",EDGE,"E21");Q27=makeQuery(id+"F16.boolean.opBoolean","INTERSECT",EDGE,{"derivedFrom":[makeQuery(id+"F12.opExtrude","SWEPT_FACE",FACE,{"disambiguationData":[OSD([sQuery(id+"F9.wireOp",EDGE,"E22")])]}),makeQuery(id+"F16.opExtrude","SWEPT_FACE",FACE,{"disambiguationData":[OSD([subQ0]),TDD([makeQuery(id+"F7.imprint","IMPRINT",EDGE,{"disambiguationData":[TD([[makeQuery(id+"F7.imprint","INTERSECT",VERTEX,{"derivedFrom":[makeQuery(id+"F1.opExtrude","CAP_EDGE",EDGE,{"disambiguationData":[OSD([sQuery(id+"F0.wireOp",EDGE,"E2")])],"isStart":false}),subQ0]}),1.0]])],"derivedFrom":subQ0})])]})]});}
            var Q28;
            Q28=makeQuery(id+"F12.opExtrude","CAP_EDGE",EDGE,{"disambiguationData":[OSD([sQuery(id+"F9.wireOp",EDGE,"E22")])],"isStart":false});
            var Q29;
            Q29=makeQuery(id+"F11.boolean.opBoolean","COPY",EDGE,{"derivedFrom":makeQuery(id+"F11.opExtrude","CAP_EDGE",EDGE,{"disambiguationData":[OSD([sQuery(id+"F9.wireOp",EDGE,"E22")])],"isStart":false})});
            var Q30;
            Q30=makeQuery(id+"F15.boolean.opBoolean","MERGE",EDGE,{"derivedFrom":[makeQuery(id+"F11.boolean.opBoolean","COPY",EDGE,{"derivedFrom":makeQuery(id+"F11.opExtrude","CAP_EDGE",EDGE,{"disambiguationData":[OSD([sQuery(id+"F9.wireOp",EDGE,"E25.3")])],"isStart":false})}),makeQuery(id+"F15.opExtrude","SWEPT_EDGE",EDGE,{"disambiguationData":[OSD([sQuery(id+"F14.wireOp",EDGE,"E35.top"),sQuery(id+"F14.wireOp",EDGE,"E35.right")])]})]});
            var Q31;
            Q31=makeQuery(id+"F15.boolean.opBoolean","MERGE",EDGE,{"derivedFrom":[makeQuery(id+"F12.opExtrude","CAP_EDGE",EDGE,{"disambiguationData":[OSD([sQuery(id+"F9.wireOp",EDGE,"E25.3")])],"isStart":false}),makeQuery(id+"F15.opExtrude","SWEPT_EDGE",EDGE,{"disambiguationData":[OSD([sQuery(id+"F14.wireOp",EDGE,"E35.bottom"),sQuery(id+"F14.wireOp",EDGE,"E35.right")])]})]});
            var Q32;
            Q32=makeQuery(id+"F11.boolean.opBoolean","COPY",EDGE,{"derivedFrom":makeQuery(id+"F11.opExtrude","SWEPT_EDGE",EDGE,{"disambiguationData":[OSD([sQuery(id+"F9.wireOp",EDGE,"E25.3"),sQuery(id+"F9.wireOp",EDGE,"E25.4")])]})});
            var Q33;
            Q33=makeQuery(id+"F11.boolean.opBoolean","COPY",EDGE,{"derivedFrom":makeQuery(id+"F11.opExtrude","SWEPT_EDGE",EDGE,{"disambiguationData":[OSD([sQuery(id+"F9.wireOp",EDGE,"E25.4"),sQuery(id+"F9.wireOp",EDGE,"E25.5")])]})});
            var Q34;
            Q34=makeQuery(id+"F12.opExtrude","CAP_EDGE",EDGE,{"disambiguationData":[OSD([sQuery(id+"F9.wireOp",EDGE,"E25.4")])],"isStart":false});
            var Q35;
            Q35=makeQuery(id+"F12.opExtrude","CAP_EDGE",EDGE,{"disambiguationData":[OSD([sQuery(id+"F9.wireOp",EDGE,"E25.5")])],"isStart":false});
            var Q36;
            Q36=makeQuery(id+"F15.boolean.opBoolean","MERGE",EDGE,{"derivedFrom":[makeQuery(id+"F12.opExtrude","CAP_EDGE",EDGE,{"disambiguationData":[OSD([sQuery(id+"F9.wireOp",EDGE,"E25.0")])],"isStart":false}),makeQuery(id+"F15.opExtrude","SWEPT_EDGE",EDGE,{"disambiguationData":[OSD([sQuery(id+"F14.wireOp",EDGE,"E35.bottom"),sQuery(id+"F14.wireOp",EDGE,"E35.left")])]})]});
            var Q37;
            Q37=makeQuery(id+"F11.boolean.opBoolean","COPY",EDGE,{"derivedFrom":makeQuery(id+"F11.opExtrude","SWEPT_EDGE",EDGE,{"disambiguationData":[OSD([sQuery(id+"F9.wireOp",EDGE,"E25.0"),sQuery(id+"F9.wireOp",EDGE,"E25.5")])]})});
            var Q38;
            Q38=makeQuery(id+"F11.boolean.opBoolean","COPY",EDGE,{"derivedFrom":makeQuery(id+"F11.opExtrude","CAP_EDGE",EDGE,{"disambiguationData":[OSD([sQuery(id+"F9.wireOp",EDGE,"E25.5")])],"isStart":false})});
            var Q39;
            Q39=makeQuery(id+"F11.boolean.opBoolean","COPY",EDGE,{"derivedFrom":makeQuery(id+"F11.opExtrude","CAP_EDGE",EDGE,{"disambiguationData":[OSD([sQuery(id+"F9.wireOp",EDGE,"E25.4")])],"isStart":false})});
            var Q40;
            Q40=makeQuery(id+"F15.boolean.opBoolean","MERGE",EDGE,{"derivedFrom":[makeQuery(id+"F11.boolean.opBoolean","COPY",EDGE,{"derivedFrom":makeQuery(id+"F11.opExtrude","CAP_EDGE",EDGE,{"disambiguationData":[OSD([sQuery(id+"F9.wireOp",EDGE,"E25.0")])],"isStart":false})}),makeQuery(id+"F15.opExtrude","SWEPT_EDGE",EDGE,{"disambiguationData":[OSD([sQuery(id+"F14.wireOp",EDGE,"E35.top"),sQuery(id+"F14.wireOp",EDGE,"E35.left")])]})]});
            var Q41;
            Q41=makeQuery(id+"F11.boolean.opBoolean","COPY",EDGE,{"derivedFrom":makeQuery(id+"F11.opExtrude","SWEPT_EDGE",EDGE,{"disambiguationData":[OSD([sQuery(id+"F9.wireOp",EDGE,"E31.MirrorCS"),sQuery(id+"F9.wireOp",EDGE,"E32.MirrorCS")])]})});
            var Q42;
            Q42=makeQuery(id+"F15.boolean.opBoolean","MERGE",EDGE,{"derivedFrom":[makeQuery(id+"F11.boolean.opBoolean","COPY",EDGE,{"derivedFrom":makeQuery(id+"F11.opExtrude","CAP_EDGE",EDGE,{"disambiguationData":[OSD([sQuery(id+"F9.wireOp",EDGE,"E32.MirrorCS")])],"isStart":false})}),makeQuery(id+"F15.opExtrude","SWEPT_EDGE",EDGE,{"disambiguationData":[OSD([sQuery(id+"F14.wireOp",EDGE,"E37.MirrorCS"),sQuery(id+"F14.wireOp",EDGE,"E38.MirrorCS")])]})]});
            var Q43;
            Q43=makeQuery(id+"F11.boolean.opBoolean","COPY",EDGE,{"derivedFrom":makeQuery(id+"F11.opExtrude","CAP_EDGE",EDGE,{"disambiguationData":[OSD([sQuery(id+"F9.wireOp",EDGE,"E31.MirrorCS")])],"isStart":false})});
            var Q44;
            Q44=makeQuery(id+"F11.boolean.opBoolean","COPY",EDGE,{"derivedFrom":makeQuery(id+"F11.opExtrude","CAP_EDGE",EDGE,{"disambiguationData":[OSD([sQuery(id+"F9.wireOp",EDGE,"E26.MirrorC")])],"isStart":false})});
            var Q45;
            Q45=makeQuery(id+"F15.boolean.opBoolean","MERGE",EDGE,{"derivedFrom":[makeQuery(id+"F12.opExtrude","CAP_EDGE",EDGE,{"disambiguationData":[OSD([sQuery(id+"F9.wireOp",EDGE,"E32.MirrorCS")])],"isStart":false}),makeQuery(id+"F15.opExtrude","SWEPT_EDGE",EDGE,{"disambiguationData":[OSD([sQuery(id+"F14.wireOp",EDGE,"E38.MirrorCS"),sQuery(id+"F14.wireOp",EDGE,"E39.MirrorCS")])]})]});
            var Q46;
            Q46=makeQuery(id+"F12.opExtrude","CAP_EDGE",EDGE,{"disambiguationData":[OSD([sQuery(id+"F9.wireOp",EDGE,"E26.MirrorC")])],"isStart":false});
            var Q47;
            Q47=makeQuery(id+"F12.opExtrude","CAP_EDGE",EDGE,{"disambiguationData":[OSD([sQuery(id+"F9.wireOp",EDGE,"E31.MirrorCS")])],"isStart":false});
            var Q48;
            Q48=makeQuery(id+"F11.boolean.opBoolean","COPY",EDGE,{"derivedFrom":makeQuery(id+"F11.opExtrude","SWEPT_EDGE",EDGE,{"disambiguationData":[OSD([sQuery(id+"F9.wireOp",EDGE,"E30.MirrorCS"),sQuery(id+"F9.wireOp",EDGE,"E31.MirrorCS")])]})});
            var Q49;
            Q49=makeQuery(id+"F11.boolean.opBoolean","COPY",EDGE,{"derivedFrom":makeQuery(id+"F11.opExtrude","SWEPT_EDGE",EDGE,{"disambiguationData":[OSD([sQuery(id+"F9.wireOp",EDGE,"E29.MirrorCS"),sQuery(id+"F9.wireOp",EDGE,"E30.MirrorCS")])]})});
            var Q50;
            Q50=makeQuery(id+"F12.opExtrude","CAP_EDGE",EDGE,{"disambiguationData":[OSD([sQuery(id+"F9.wireOp",EDGE,"E30.MirrorCS")])],"isStart":false});
            var Q51;
            Q51=makeQuery(id+"F15.boolean.opBoolean","MERGE",EDGE,{"derivedFrom":[makeQuery(id+"F12.opExtrude","CAP_EDGE",EDGE,{"disambiguationData":[OSD([sQuery(id+"F9.wireOp",EDGE,"E29.MirrorCS")])],"isStart":false}),makeQuery(id+"F15.opExtrude","SWEPT_EDGE",EDGE,{"disambiguationData":[OSD([sQuery(id+"F14.wireOp",EDGE,"E39.MirrorCS"),sQuery(id+"F14.wireOp",EDGE,"E40.MirrorCS")])]})]});
            var Q52;
            Q52=makeQuery(id+"F11.boolean.opBoolean","COPY",EDGE,{"derivedFrom":makeQuery(id+"F11.opExtrude","CAP_EDGE",EDGE,{"disambiguationData":[OSD([sQuery(id+"F9.wireOp",EDGE,"E30.MirrorCS")])],"isStart":false})});
            var Q53;
            Q53=makeQuery(id+"F15.boolean.opBoolean","MERGE",EDGE,{"derivedFrom":[makeQuery(id+"F11.boolean.opBoolean","COPY",EDGE,{"derivedFrom":makeQuery(id+"F11.opExtrude","CAP_EDGE",EDGE,{"disambiguationData":[OSD([sQuery(id+"F9.wireOp",EDGE,"E29.MirrorCS")])],"isStart":false})}),makeQuery(id+"F15.opExtrude","SWEPT_EDGE",EDGE,{"disambiguationData":[OSD([sQuery(id+"F14.wireOp",EDGE,"E37.MirrorCS"),sQuery(id+"F14.wireOp",EDGE,"E40.MirrorCS")])]})]});
            var Q54;
            Q54=makeQuery(id+"F10.boolean.opBoolean","COPY",EDGE,{"derivedFrom":makeQuery(id+"F10.opExtrude","CAP_EDGE",EDGE,{"disambiguationData":[OSD([sQuery(id+"F9.wireOp",EDGE,"E26.MirrorC")])],"isStart":false})});
            var Q55;
            Q55=makeQuery(id+"F10.boolean.opBoolean","COPY",EDGE,{"derivedFrom":makeQuery(id+"F10.opExtrude","CAP_EDGE",EDGE,{"disambiguationData":[OSD([sQuery(id+"F9.wireOp",EDGE,"E22")])],"isStart":false})});
            var Q56;
            Q56=makeQuery(id+"F13.boolean.opBoolean","COPY",EDGE,{"derivedFrom":makeQuery(id+"F13.opExtrude","CAP_EDGE",EDGE,{"disambiguationData":[OSD([sQuery(id+"F9.wireOp",EDGE,"E24")])],"isStart":false})});
            var Q57;
            Q57=makeQuery(id+"F13.boolean.opBoolean","COPY",EDGE,{"derivedFrom":makeQuery(id+"F13.opExtrude","CAP_EDGE",EDGE,{"disambiguationData":[OSD([sQuery(id+"F9.wireOp",EDGE,"E34.MirrorC")])],"isStart":false})});
            fillet(context, id + "F19", {"entities" : qUnion([Q0, Q1, Q2, Q3, Q4, Q5, Q6, Q7, Q8, Q9, Q10, Q11, Q12, Q13, Q14, Q15, Q16, Q17, Q18, Q19, Q20, Q21, Q22, Q23, Q24, Q25, Q26, Q27, Q28, Q29, Q30, Q31, Q32, Q33, Q34, Q35, Q36, Q37, Q38, Q39, Q40, Q41, Q42, Q43, Q44, Q45, Q46, Q47, Q48, Q49, Q50, Q51, Q52, Q53, Q54, Q55, Q56, Q57]), "radius" : 0.5 * mm, "tangentPropagation" : true, "allowEdgeOverflow" : false});
        }
        {
            var Q0;
            Q0=makeQuery(id+"F4.boolean.opBoolean","COPY",EDGE,{"derivedFrom":makeQuery(id+"F4.opExtrude","SWEPT_EDGE",EDGE,{"disambiguationData":[OSD([sQuery(id+"F0.wireOp",EDGE,"E3"),sQuery(id+"F0.wireOp",EDGE,"E4"),sQuery(id+"F2.wireOp",EDGE,"E11"),sQuery(id+"F2.wireOp",EDGE,"E14")])]})});
            var Q1;
            Q1=makeQuery(id+"F3.boolean.opBoolean","COPY",EDGE,{"derivedFrom":makeQuery(id+"F3.opExtrude","CAP_EDGE",EDGE,{"disambiguationData":[OSD([sQuery(id+"F2.wireOp",EDGE,"E7")])],"isStart":true})});
            var Q2;
            {var subQ0=sQuery(id+"F2.wireOp",EDGE,"E11");var subQ1=sQuery(id+"F2.wireOp",EDGE,"E12");var subQ2=sQuery(id+"F2.wireOp",EDGE,"E8");var subQ3=sQuery(id+"F2.wireOp",EDGE,"E7");Q2=makeQuery(id+"F18.opFillet","BLEND_EDGE",EDGE,{"blendedFrom":[makeQuery(id+"F4.boolean.opBoolean","COPY",EDGE,{"derivedFrom":makeQuery(id+"F4.opExtrude","CAP_EDGE",EDGE,{"disambiguationData":[OSD([subQ0])],"isStart":true})}),makeQuery(id+"F4.boolean.opBoolean","SPLIT",FACE,{"disambiguationData":[TD([makeQuery(id+"F3.boolean.opBoolean","COPY",FACE,{"derivedFrom":makeQuery(id+"F3.opExtrude","SWEPT_FACE",FACE,{"disambiguationData":[OSD([subQ3])]})})])],"derivedFrom":makeQuery(id+"F3.boolean.opBoolean","COPY",FACE,{"derivedFrom":makeQuery(id+"F3.opExtrude","SWEPT_FACE",FACE,{"disambiguationData":[OSD([subQ2,subQ1])]})})})],"blendedInto":[makeQuery(id+"F4.boolean.opBoolean","SPLIT",FACE,{"disambiguationData":[TD([makeQuery(id+"F3.boolean.opBoolean","COPY",FACE,{"derivedFrom":makeQuery(id+"F3.opExtrude","SWEPT_FACE",FACE,{"disambiguationData":[OSD([subQ3])]})})])],"derivedFrom":makeQuery(id+"F3.boolean.opBoolean","COPY",FACE,{"derivedFrom":makeQuery(id+"F3.opExtrude","SWEPT_FACE",FACE,{"disambiguationData":[OSD([subQ2,subQ1])]})})})]});}
            var Q3;
            {var subQ0=sQuery(id+"F2.wireOp",EDGE,"E11");var subQ1=sQuery(id+"F2.wireOp",EDGE,"E14");Q3=makeQuery(id+"F6.boolean.opBoolean","SPLIT",EDGE,{"disambiguationData":[TD([makeQuery(id+"F4.boolean.opBoolean","COPY",FACE,{"derivedFrom":makeQuery(id+"F4.opExtrude","SWEPT_FACE",FACE,{"disambiguationData":[OSD([subQ0])]})})])],"derivedFrom":makeQuery(id+"F4.boolean.opBoolean","COPY",EDGE,{"derivedFrom":makeQuery(id+"F4.opExtrude","CAP_EDGE",EDGE,{"disambiguationData":[OSD([subQ1])],"isStart":false})})});}
            var Q4;
            {var subQ1=sQuery(id+"F2.wireOp",EDGE,"E10");var subQ2=sQuery(id+"F2.wireOp",EDGE,"E7");Q4=makeQuery(id+"F6.boolean.opBoolean","SPLIT",EDGE,{"disambiguationData":[TD([makeQuery(id+"F3.boolean.opBoolean","COPY",FACE,{"derivedFrom":makeQuery(id+"F3.opExtrude","SWEPT_FACE",FACE,{"disambiguationData":[OSD([subQ2])]})})])],"derivedFrom":makeQuery(id+"F3.boolean.opBoolean","COPY",EDGE,{"derivedFrom":makeQuery(id+"F3.opExtrude","CAP_EDGE",EDGE,{"disambiguationData":[OSD([subQ1])],"isStart":false})})});}
            var Q5;
            Q5=makeQuery(id+"F3.boolean.opBoolean","COPY",EDGE,{"derivedFrom":makeQuery(id+"F3.opExtrude","SWEPT_EDGE",EDGE,{"disambiguationData":[OSD([sQuery(id+"F2.wireOp",EDGE,"E7"),sQuery(id+"F2.wireOp",EDGE,"E10")])]})});
            var Q6;
            Q6=makeQuery(id+"F3.boolean.opBoolean","COPY",EDGE,{"derivedFrom":makeQuery(id+"F3.opExtrude","CAP_EDGE",EDGE,{"disambiguationData":[OSD([sQuery(id+"F2.wireOp",EDGE,"E7")])],"isStart":false})});
            var Q7;
            {var subQ0=sQuery(id+"F2.wireOp",EDGE,"E13");var subQ1=sQuery(id+"F2.wireOp",EDGE,"E14");Q7=makeQuery(id+"F6.boolean.opBoolean","SPLIT",EDGE,{"disambiguationData":[TD([makeQuery(id+"F4.boolean.opBoolean","COPY",FACE,{"derivedFrom":makeQuery(id+"F4.opExtrude","SWEPT_FACE",FACE,{"disambiguationData":[OSD([subQ0])]})})])],"derivedFrom":makeQuery(id+"F4.boolean.opBoolean","COPY",EDGE,{"derivedFrom":makeQuery(id+"F4.opExtrude","CAP_EDGE",EDGE,{"disambiguationData":[OSD([subQ1])],"isStart":false})})});}
            var Q8;
            {var subQ1=sQuery(id+"F2.wireOp",EDGE,"E9");var subQ2=sQuery(id+"F2.wireOp",EDGE,"E10");Q8=makeQuery(id+"F6.boolean.opBoolean","SPLIT",EDGE,{"disambiguationData":[TD([makeQuery(id+"F3.boolean.opBoolean","COPY",FACE,{"derivedFrom":makeQuery(id+"F3.opExtrude","SWEPT_FACE",FACE,{"disambiguationData":[OSD([subQ1])]})})])],"derivedFrom":makeQuery(id+"F3.boolean.opBoolean","COPY",EDGE,{"derivedFrom":makeQuery(id+"F3.opExtrude","CAP_EDGE",EDGE,{"disambiguationData":[OSD([subQ2])],"isStart":false})})});}
            var Q9;
            Q9=makeQuery(id+"F4.boolean.opBoolean","COPY",EDGE,{"derivedFrom":makeQuery(id+"F4.opExtrude","SWEPT_EDGE",EDGE,{"disambiguationData":[OSD([sQuery(id+"F0.wireOp",EDGE,"E3"),sQuery(id+"F0.wireOp",EDGE,"E4"),sQuery(id+"F2.wireOp",EDGE,"E13"),sQuery(id+"F2.wireOp",EDGE,"E14")])]})});
            var Q10;
            Q10=makeQuery(id+"F1.opExtrude","SWEPT_EDGE",EDGE,{"disambiguationData":[OSD([sQuery(id+"F0.wireOp",EDGE,"E2"),sQuery(id+"F0.wireOp",EDGE,"E3")])]});
            var Q11;
            {var subQ0=sQuery(id+"F0.wireOp",EDGE,"E3");var subQ1=makeQuery(id+"F1.opExtrude","SWEPT_FACE",FACE,{"disambiguationData":[OSD([subQ0])]});var subQ2=sQuery(id+"F0.wireOp",EDGE,"E2");var subQ4=makeQuery(id+"F1.opExtrude","CAP_EDGE",EDGE,{"disambiguationData":[OSD([subQ2])],"isStart":false});Q11=makeQuery(id+"F18.opFillet","BLEND_EDGE",EDGE,{"blendedFrom":[makeQuery(id+"F16.boolean.opBoolean","SPLIT",EDGE,{"disambiguationData":[TD([subQ1])],"derivedFrom":subQ4}),subQ1],"blendedInto":[subQ1]});}
            var Q12;
            {var subQ0=sQuery(id+"F0.wireOp",EDGE,"E3");var subQ1=makeQuery(id+"F1.opExtrude","SWEPT_FACE",FACE,{"disambiguationData":[OSD([subQ0])]});var subQ2=sQuery(id+"F0.wireOp",EDGE,"E2");var subQ4=makeQuery(id+"F1.opExtrude","CAP_EDGE",EDGE,{"disambiguationData":[OSD([subQ2])],"isStart":true});Q12=makeQuery(id+"F18.opFillet","BLEND_EDGE",EDGE,{"blendedFrom":[makeQuery(id+"F16.boolean.opBoolean","SPLIT",EDGE,{"disambiguationData":[TD([subQ1])],"derivedFrom":subQ4}),subQ1],"blendedInto":[subQ1]});}
            var Q13;
            {var subQ0=sQuery(id+"F2.wireOp",EDGE,"E12");var subQ1=sQuery(id+"F2.wireOp",EDGE,"E8");Q13=makeQuery(id+"F4.boolean.opBoolean","SPLIT",EDGE,{"disambiguationData":[TD([makeQuery(id+"F3.boolean.opBoolean","COPY",FACE,{"derivedFrom":makeQuery(id+"F3.opExtrude","SWEPT_FACE",FACE,{"disambiguationData":[OSD([sQuery(id+"F2.wireOp",EDGE,"E9")])]})})])],"derivedFrom":makeQuery(id+"F3.boolean.opBoolean","COPY",EDGE,{"derivedFrom":makeQuery(id+"F3.opExtrude","CAP_EDGE",EDGE,{"disambiguationData":[OSD([subQ1,subQ0])],"isStart":true})})});}
            var Q14;
            Q14=makeQuery(id+"F3.boolean.opBoolean","COPY",EDGE,{"derivedFrom":makeQuery(id+"F3.opExtrude","CAP_EDGE",EDGE,{"disambiguationData":[OSD([sQuery(id+"F2.wireOp",EDGE,"E9")])],"isStart":true})});
            var Q15;
            Q15=makeQuery(id+"F3.boolean.opBoolean","COPY",EDGE,{"derivedFrom":makeQuery(id+"F3.opExtrude","CAP_EDGE",EDGE,{"disambiguationData":[OSD([sQuery(id+"F2.wireOp",EDGE,"E9")])],"isStart":false})});
            var Q16;
            Q16=makeQuery(id+"F3.boolean.opBoolean","COPY",EDGE,{"derivedFrom":makeQuery(id+"F3.opExtrude","SWEPT_EDGE",EDGE,{"disambiguationData":[OSD([sQuery(id+"F2.wireOp",EDGE,"E8"),sQuery(id+"F2.wireOp",EDGE,"E9")])]})});
            var Q17;
            {var subQ1=sQuery(id+"F2.wireOp",EDGE,"E12");var subQ2=sQuery(id+"F2.wireOp",EDGE,"E9");var subQ3=sQuery(id+"F2.wireOp",EDGE,"E8");Q17=makeQuery(id+"F4.boolean.opBoolean","SPLIT",EDGE,{"disambiguationData":[TD([makeQuery(id+"F3.boolean.opBoolean","COPY",FACE,{"derivedFrom":makeQuery(id+"F3.opExtrude","SWEPT_FACE",FACE,{"disambiguationData":[OSD([subQ2])]})})])],"derivedFrom":makeQuery(id+"F3.boolean.opBoolean","COPY",EDGE,{"derivedFrom":makeQuery(id+"F3.opExtrude","CAP_EDGE",EDGE,{"disambiguationData":[OSD([subQ3,subQ1])],"isStart":false})})});}
            var Q18;
            Q18=makeQuery(id+"F3.boolean.opBoolean","COPY",EDGE,{"derivedFrom":makeQuery(id+"F3.opExtrude","SWEPT_EDGE",EDGE,{"disambiguationData":[OSD([sQuery(id+"F2.wireOp",EDGE,"E7"),sQuery(id+"F2.wireOp",EDGE,"E8")])]})});
            var Q19;
            {var subQ1=sQuery(id+"F2.wireOp",EDGE,"E12");var subQ2=sQuery(id+"F2.wireOp",EDGE,"E8");var subQ3=sQuery(id+"F2.wireOp",EDGE,"E7");Q19=makeQuery(id+"F4.boolean.opBoolean","SPLIT",EDGE,{"disambiguationData":[TD([makeQuery(id+"F3.boolean.opBoolean","COPY",FACE,{"derivedFrom":makeQuery(id+"F3.opExtrude","SWEPT_FACE",FACE,{"disambiguationData":[OSD([subQ3])]})})])],"derivedFrom":makeQuery(id+"F3.boolean.opBoolean","COPY",EDGE,{"derivedFrom":makeQuery(id+"F3.opExtrude","CAP_EDGE",EDGE,{"disambiguationData":[OSD([subQ2,subQ1])],"isStart":false})})});}
            var Q20;
            Q20=makeQuery(id+"F3.boolean.opBoolean","COPY",EDGE,{"derivedFrom":makeQuery(id+"F3.opExtrude","SWEPT_EDGE",EDGE,{"disambiguationData":[OSD([sQuery(id+"F2.wireOp",EDGE,"E9"),sQuery(id+"F2.wireOp",EDGE,"E10")])]})});
            fillet(context, id + "F20", {"entities" : qUnion([Q0, Q1, Q2, Q3, Q4, Q5, Q6, Q7, Q8, Q9, Q10, Q11, Q12, Q13, Q14, Q15, Q16, Q17, Q18, Q19, Q20]), "radius" : 1 * mm, "tangentPropagation" : true, "allowEdgeOverflow" : false});
        }
    });
